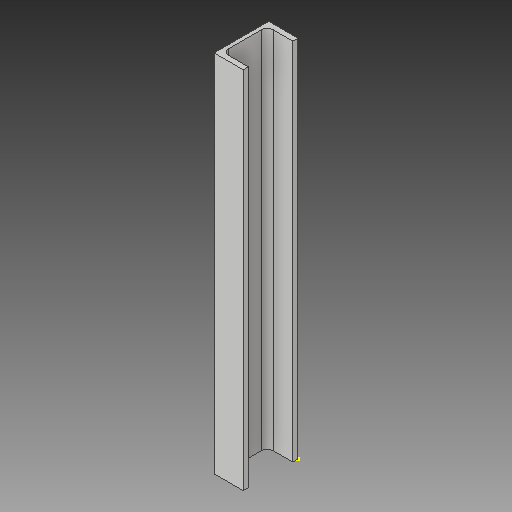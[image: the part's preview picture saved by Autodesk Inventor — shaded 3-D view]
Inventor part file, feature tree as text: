
AUTODESK INVENTOR PART (.ipt)
format: ipt  version: 2019 (Build 230136000, 136)  size: 93,184 bytes
history: native  units: in
note: dims shown in document units (in); Inventor stores cm internally (conversion verified against a paired STEP export)
features: other x3, sketch x2
ambient origin geometry x8: Origin, YZ Plane, XZ Plane, XY Plane, X Axis, Y Axis, Z Axis, Center Point
bodies: Solid1 (feature_tree)
feature tree (5):
  other  "Channel2.ipt"
  other  "Solid1::Channel2.ipt"
  other  "TaggingFeature1"
  sketch  "Sketch1"  dims[d0=0.3937in]
  sketch  "Sketch2"
